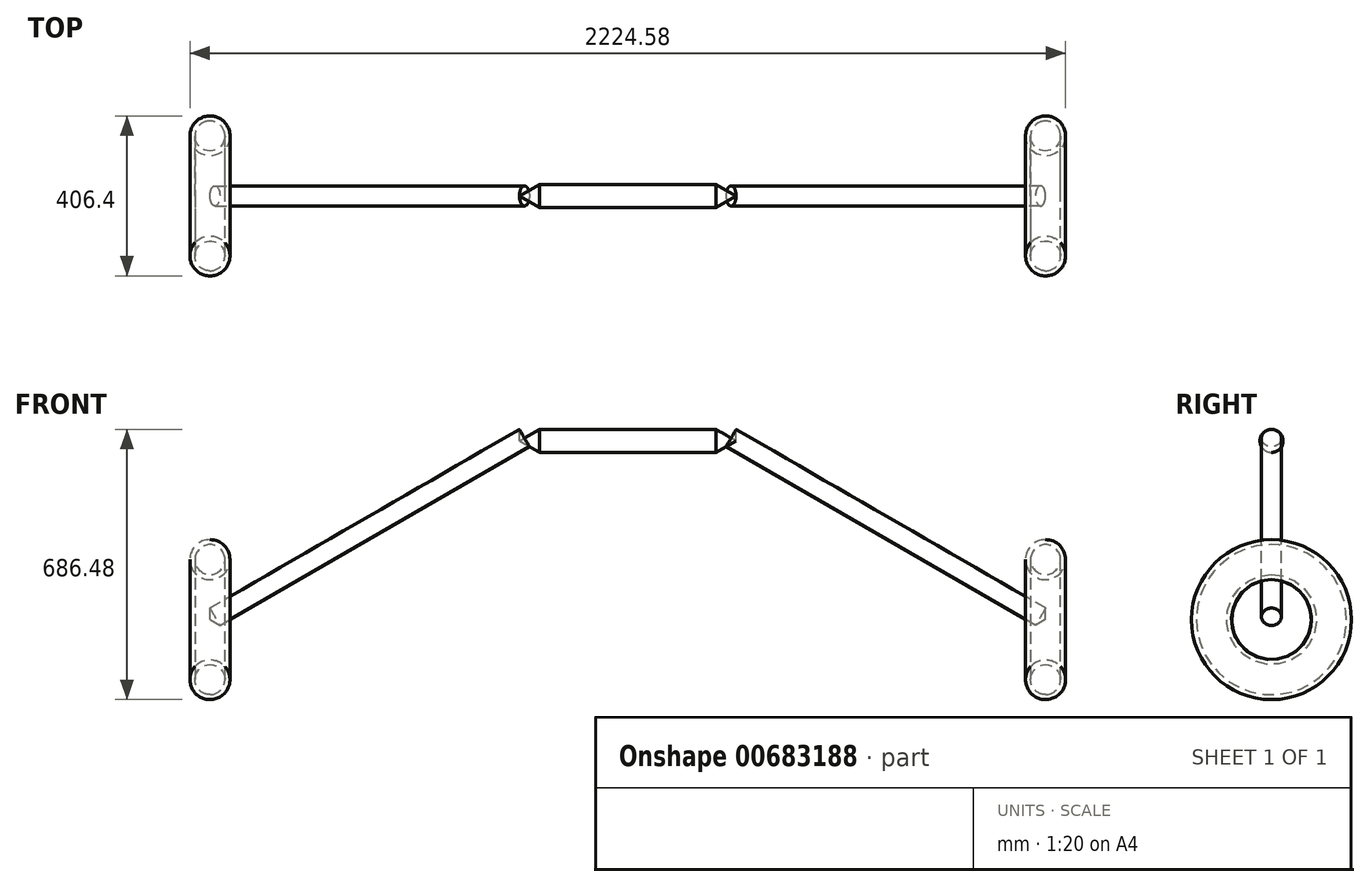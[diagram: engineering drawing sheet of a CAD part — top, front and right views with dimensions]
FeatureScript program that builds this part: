
annotation { "Feature Type Name" : "Feature", "Feature Type Description" : "" }
export const myFeature = defineFeature(function(context is Context, id is Id, definition is map)
    precondition{}
    {
        {
            var Q0;
            Q0=qCreatedBy(makeId("Front.planeOp"),FACE);
            var sketch = newSketch(context, id + "F0", { "sketchPlane" : qUnion([Q0])});
            skLineSegment(sketch, "E0", {"start": v(-1061.5, 0) * mm, "end": v(0, 612.85) * mm});
            skLineSegment(sketch, "E1", {"start": v(0, 612.85) * mm, "end": v(1061.5, 0) * mm});
            skLineSegment(sketch, "E2", {"start": v(-1061.5, 0) * mm, "end": v(1061.5, 0) * mm, "construction": true});
            skPoint(sketch, "E3", {"position": v(0, 0) * mm});
            skCircle(sketch, "E4", {"center": v(1061.5, 152.4) * mm, "radius": 50.8 * mm});
            skCircle(sketch, "E5", {"center": v(-1061.5, 152.4) * mm, "radius": 50.8 * mm});
            skLineSegment(sketch, "E6", {"start": v(1061.5, 0) * mm, "end": v(1061.5, 152.4) * mm});
            skLineSegment(sketch, "E7", {"start": v(-1061.5, 0) * mm, "end": v(-1061.5, 152.4) * mm});
            skCircle(sketch, "E8", {"center": v(-1061.5, 152.4) * mm, "radius": 38.1 * mm});
            skCircle(sketch, "E9", {"center": v(1061.5, 152.4) * mm, "radius": 38.1 * mm});
            skLineSegment(sketch, "E10.bottom", {"start": v(275.23, 453.95) * mm, "end": v(-275.23, 453.95) * mm});
            skLineSegment(sketch, "E10.top", {"start": v(275.23, 612.85) * mm, "end": v(-275.23, 612.85) * mm});
            skLineSegment(sketch, "E10.left", {"start": v(275.23, 453.95) * mm, "end": v(275.23, 612.85) * mm});
            skLineSegment(sketch, "E10.right", {"start": v(-275.23, 453.95) * mm, "end": v(-275.23, 612.85) * mm});
            skPoint(sketch, "E11", {"position": v(0, 612.85) * mm});
            skLineSegment(sketch, "E12", {"start": v(1061.5, 29.33) * mm, "end": v(275.23, 483.28) * mm});
            skLineSegment(sketch, "E13", {"start": v(275.23, 483.28) * mm, "end": v(-275.23, 483.28) * mm});
            skSolve(sketch);
        }
        {
            var Q0;
            Q0=makeQuery(id+"F0.imprint","IMPRINT",FACE,{"disambiguationData":[TD([[makeQuery(id+"F0.imprint","IMPRINT",EDGE,{"derivedFrom":sQuery(id+"F0.wireOp",EDGE,"E5")}),1.0]])]});
            var Q1;
            Q1=makeQuery(id+"F0.imprint","IMPRINT",FACE,{"disambiguationData":[TD([[makeQuery(id+"F0.imprint","IMPRINT",EDGE,{"derivedFrom":sQuery(id+"F0.wireOp",EDGE,"E4")}),1.0]])]});
            var Q2;
            Q2=sQuery(id+"F0.wireOp",EDGE,"E2");
            revolve(context, id + "F1", {"entities" : qUnion([Q0, Q1]), "axis" : qUnion([Q2]), "revolveType" : RevolveType.FULL});
        }
        {
            var Q0;
            {var subQ5=sQuery(id+"F0.wireOp",EDGE,"E12");Q0=makeQuery(id+"F0.imprint","IMPRINT",FACE,{"disambiguationData":[TD([[makeQuery(id+"F0.imprint","IMPRINT",EDGE,{"derivedFrom":subQ5}),1.0]])]});}
            var Q1;
            Q1=sQuery(id+"F0.wireOp",EDGE,"E12");
            var Q2;
            Q2=sQuery(id+"F0.wireOp",EDGE,"E1");
            revolve(context, id + "F2", {"entities" : qUnion([Q0]), "surfaceEntities" : qUnion([Q1]), "axis" : qUnion([Q2]), "revolveType" : RevolveType.FULL});
        }
        {
            var Q0;
            Q0=makeQuery(id+"F2.opRevolve","SWEPT_BODY",BODY,{"disambiguationData":[OSD([sQuery(id+"F0.wireOp",EDGE,"E1"),sQuery(id+"F0.wireOp",EDGE,"E6"),sQuery(id+"F0.wireOp",EDGE,"E10.left"),sQuery(id+"F0.wireOp",EDGE,"E12")])]});
            var Q1;
            Q1=qCreatedBy(makeId("Right.planeOp"),FACE);
            mirror(context, id + "F3", {"entities" : qUnion([Q0]), "mirrorPlane" : qUnion([Q1])});
        }
        {
            var Q0;
            {var subQ0=sQuery(id+"F0.wireOp",EDGE,"E10.bottom");Q0=makeQuery(id+"F0.imprint","IMPRINT",FACE,{"disambiguationData":[TD([[makeQuery(id+"F0.imprint","IMPRINT",EDGE,{"derivedFrom":subQ0}),-1.0]])]});}
            var Q1;
            Q1=sQuery(id+"F0.wireOp",EDGE,"E10.bottom");
            revolve(context, id + "F4", {"entities" : qUnion([Q0]), "axis" : qUnion([Q1]), "revolveType" : RevolveType.FULL});
        }
    });
